# Revit family: Door_Service_BetweenJambMount_Cookson
name_source: partatom
category: Doors
revit_build: Autodesk Revit MEP 2013 (Build: 20130531_2115(x64)
units: mm (PartAtom-declared; Revit-internal decimal feet)

## types (12) — shared parameters
04 CSI = 08 33 00
95 CSI = 08330
A = 1' - 4"
Assembly Code = B2030410
B = 1' - 6"
C = 0' - 5"
Coil Dimension Note = 14In to 22In -  Consult Cookson when dimensions are critical
Cost Note = Based on size, materials selected. Consult Cookson
D = 0' - 7"
Description = Built to order metal slatted rolling doors provide security against entry and/or weather protection.
Distributor Locator = http://www.cooksondoor.com
Exterior Wall Offset = 0' - 0 1/4"
From Coil Side Operate on Left = No
From Coil Side Operate on Right = Yes
Function = Interior
Guide Height = 11' - 11 1/128"
Height = 11' - 6 1/128"
Jamb Dimension Note = 6 3/4In - 10 1/4In wide.  Consult Cookson when dimensions are critical
LEED Information = http://www.cooksondoor.com
Largest Dimension = 10' - 0"
Manufacturer = CornellCookson,Inc.
Model = ESD10
Mounting = Face of Wall
Opening Height = 10' - 0"
Opening Width = 8' - 0"
Operator Width = 8' - 10 1/2"
Optional Operator Cover Left = No
Optional Operator Cover Right = No
Optional Powder Coated Finish, standard RAL colors, Galv. Steel and Aluminum only = No
Optional aluminum, color anodized finish = No
Pull Height = 7' - 8 1/256"
Representative Disclaimer = Cookson products are sold and installed through a nationwide network of independent distributors.
Revit Object Download Link = http://cornellcookson.smartbim.com
Rough Height = 5' - 7 1/2"
Sizing Disclaimer = 30’ wide, 30’ high standard construction. Larger Openings possible, consult factory
Subcategory = Roll Up
Thickness = 5' - 11 1/2"
URL = http://www.cooksondoor.com
URL CAD = http://www.cooksondoor.com
URL Photographs = http://www.cooksondoor.com
URL Specifications = http://www.cooksondoor.com
Wall Closure = By host
Wall Construction = Masonry, Steel or Wood
Width = 9' - 3"
Windload = A full range of specific wind load requirements available- Consult Cookson
Zone 1 = No
Zone 10 = No
Zone 11 = No
Zone 2 = No
Zone 3 = Yes
Zone 4 = No
Zone 5 = No
Zone 6 = No
Zone 7 = No
Zone 8 = No
Zone 9 = No
zero-valued in all types: Cost

## per-type parameters (varying)
| type | Bottom Bar | Chain | Curtain 2 5/8" Slat | Guides | Hood | Motor | Operator | Push |
| Hand-Chain Operated, Aluminium (Anodized Finish) | Aluminum, mill finish (non-curtain components) | Yes | Aluminum, mill finish (curtain only) | Aluminum, mill finish (non-curtain components) | Aluminum, mill finish (non-curtain components) | No | Operator : Hand-Chain | No |
| Hand-Chain Operated, Aluminium (Mill Finish) | Aluminum, mill finish (non-curtain components) | Yes | Aluminum, mill finish (curtain only) | Aluminum, mill finish (non-curtain components) | Aluminum, mill finish (non-curtain components) | No | Operator : Hand-Chain | No |
| Hand-Chain Operated, Galvanized Steel | Galvanized or powder coated plain steel (non curtain components) | Yes | Galvanized steel (curtain only) | Galvanized or powder coated plain steel (non curtain components) | Galvanized or powder coated plain steel (non curtain components) | No | Operator : Hand-Chain | No |
| Hand-Chain Operated, Stainless Steel | Stainless steel (non-curtain components) | Yes | Stainless steel (curtain only) | Stainless steel (non-curtain components) | Stainless steel (non-curtain components) | No | Operator : Hand-Chain | No |
| Motor Operated, Aluminium (Anodized Finish) | Aluminum, anodized finish (non-curtain components) | No | Aluminum, anodized finish (curtain only) | Aluminum, anodized finish (non-curtain components) | Stainless steel (non-curtain components) | Yes | Operator : Motor Operator | No |
| Motor Operated, Aluminium (Mill Finish) | Aluminum, mill finish (non-curtain components) | No | Aluminum, mill finish (curtain only) | Aluminum, mill finish (non-curtain components) | Aluminum, mill finish (non-curtain components) | Yes | Operator : Motor Operator | No |
| Motor Operated, Galvanized Steel | Galvanized or powder coated plain steel (non curtain components) | No | Galvanized steel (curtain only) | Galvanized or powder coated plain steel (non curtain components) | Galvanized or powder coated plain steel (non curtain components) | Yes | Operator : Motor Operator | No |
| Motor Operated, Stainless Steel | Stainless steel (non-curtain components) | No | Stainless steel (curtain only) | Stainless steel (non-curtain components) | Stainless steel (non-curtain components) | Yes | Operator : Motor Operator | No |
| Push-Up Operated, Aluminium (Anodized Finish) | Aluminum, anodized finish (non-curtain components) | No | Aluminum, anodized finish (curtain only) | Aluminum, anodized finish (non-curtain components) | Aluminum, anodized finish (non-curtain components) | No | Operator : Push-UP | Yes |
| Push-Up Operated, Aluminium (Mill Finish) | Aluminum, mill finish (non-curtain components) | No | Aluminum, mill finish (curtain only) | Aluminum, mill finish (non-curtain components) | Aluminum, mill finish (non-curtain components) | No | Operator : Push-UP | Yes |
| Push-Up Operated, Galvanized Steel | Galvanized or powder coated plain steel (non curtain components) | No | Galvanized steel (curtain only) | Galvanized or powder coated plain steel (non curtain components) | Galvanized or powder coated plain steel (non curtain components) | No | Operator : Push-UP | Yes |
| Push-Up Operated, Stainless Steel | Stainless steel (non-curtain components) | No | Stainless steel (curtain only) | Stainless steel (non-curtain components) | Stainless steel (non-curtain components) | No | Operator : Push-UP | Yes |

## geometry (parser evidence)
native form markers: Blend x24, Sweep x15
no freeform markers — native parametric forms only
